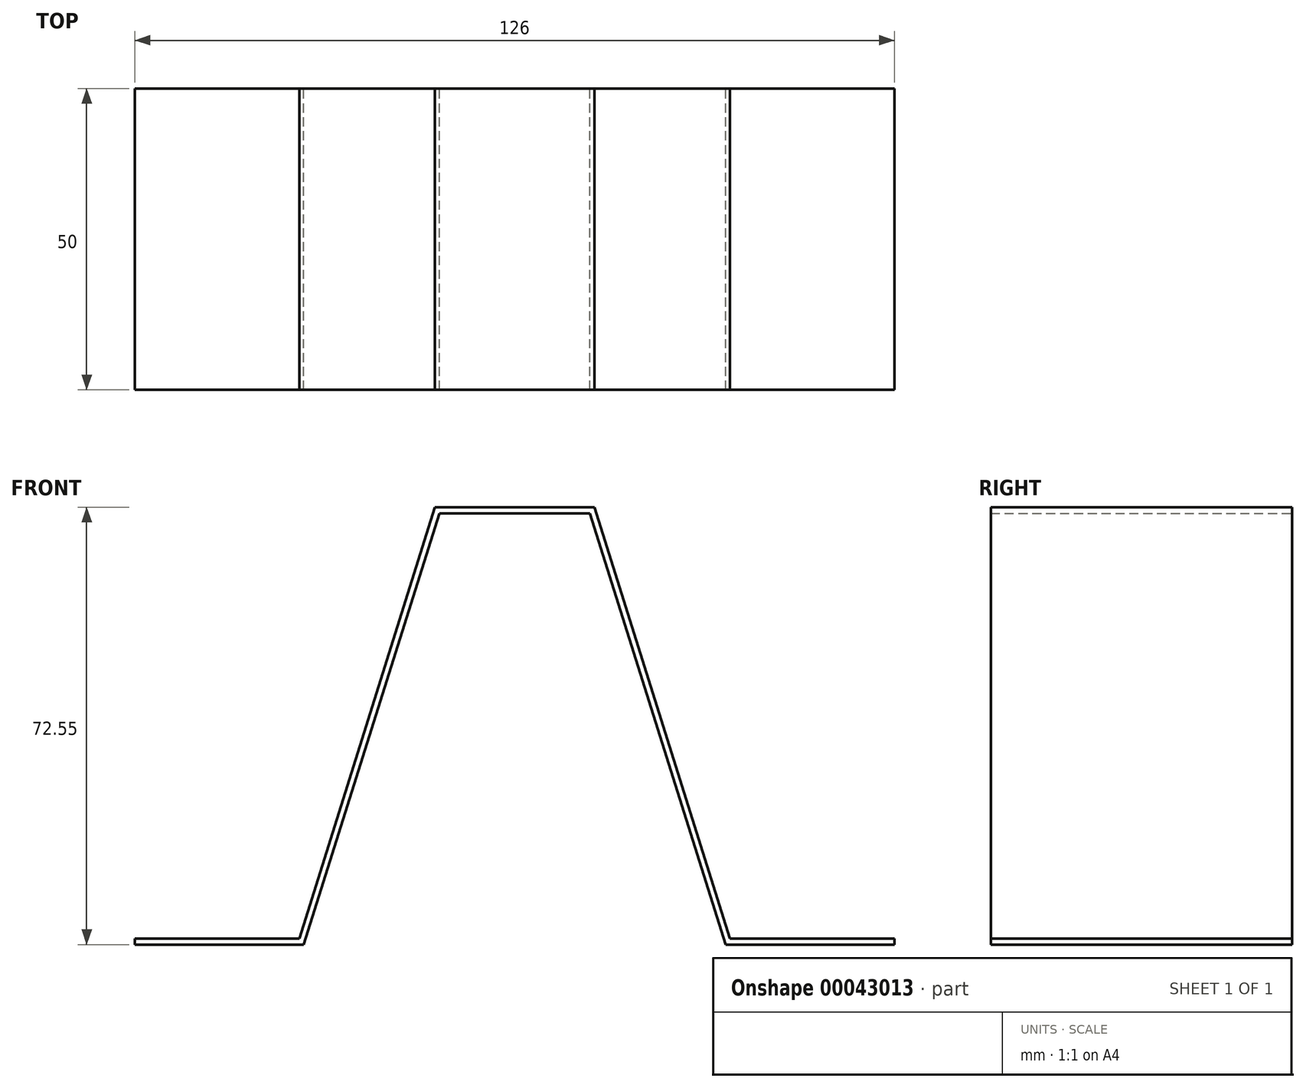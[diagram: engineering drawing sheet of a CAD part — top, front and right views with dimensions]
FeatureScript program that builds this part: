
annotation { "Feature Type Name" : "Feature", "Feature Type Description" : "" }
export const myFeature = defineFeature(function(context is Context, id is Id, definition is map)
    precondition{}
    {
        {
            var Q0;
            Q0=qCreatedBy(makeId("Front.planeOp"),FACE);
            var sketch = newSketch(context, id + "F0", { "sketchPlane" : qUnion([Q0])});
            skLineSegment(sketch, "E0", {"start": v(0, 71.55) * mm, "end": v(-12.5, 71.55) * mm});
            skLineSegment(sketch, "E1", {"start": v(-12.5, 71.55) * mm, "end": v(-35, 0) * mm});
            skLineSegment(sketch, "E2", {"start": v(-35, 0) * mm, "end": v(-63, 0) * mm});
            skLineSegment(sketch, "E3.0", {"start": v(-35.73, 1) * mm, "end": v(-63, 1) * mm});
            skLineSegment(sketch, "E3.1", {"start": v(-13.23, 72.55) * mm, "end": v(-35.73, 1) * mm});
            skLineSegment(sketch, "E3.2", {"start": v(0, 72.55) * mm, "end": v(-13.23, 72.55) * mm});
            skLineSegment(sketch, "E4", {"start": v(-63, 1) * mm, "end": v(-63, 0) * mm});
            skLineSegment(sketch, "E5.MirrorCS", {"start": v(63, 1) * mm, "end": v(63, 0) * mm});
            skLineSegment(sketch, "E6.MirrorCS", {"start": v(35.73, 1) * mm, "end": v(63, 1) * mm});
            skLineSegment(sketch, "E7.MirrorCS", {"start": v(13.23, 72.55) * mm, "end": v(35.73, 1) * mm});
            skLineSegment(sketch, "E8.MirrorCS", {"start": v(0, 71.55) * mm, "end": v(12.5, 71.55) * mm});
            skLineSegment(sketch, "E9.MirrorCS", {"start": v(0, 72.55) * mm, "end": v(13.23, 72.55) * mm});
            skLineSegment(sketch, "E10.MirrorCS", {"start": v(35, 0) * mm, "end": v(63, 0) * mm});
            skLineSegment(sketch, "E11.MirrorCS", {"start": v(12.5, 71.55) * mm, "end": v(35, 0) * mm});
            skSolve(sketch);
        }
        {
            var Q0;
            Q0 = qSketchRegion(id + "F0", true);
            extrude(context, id + "F1", {"entities" : qUnion([Q0]), "depth" : 50 * mm});
        }
    });
